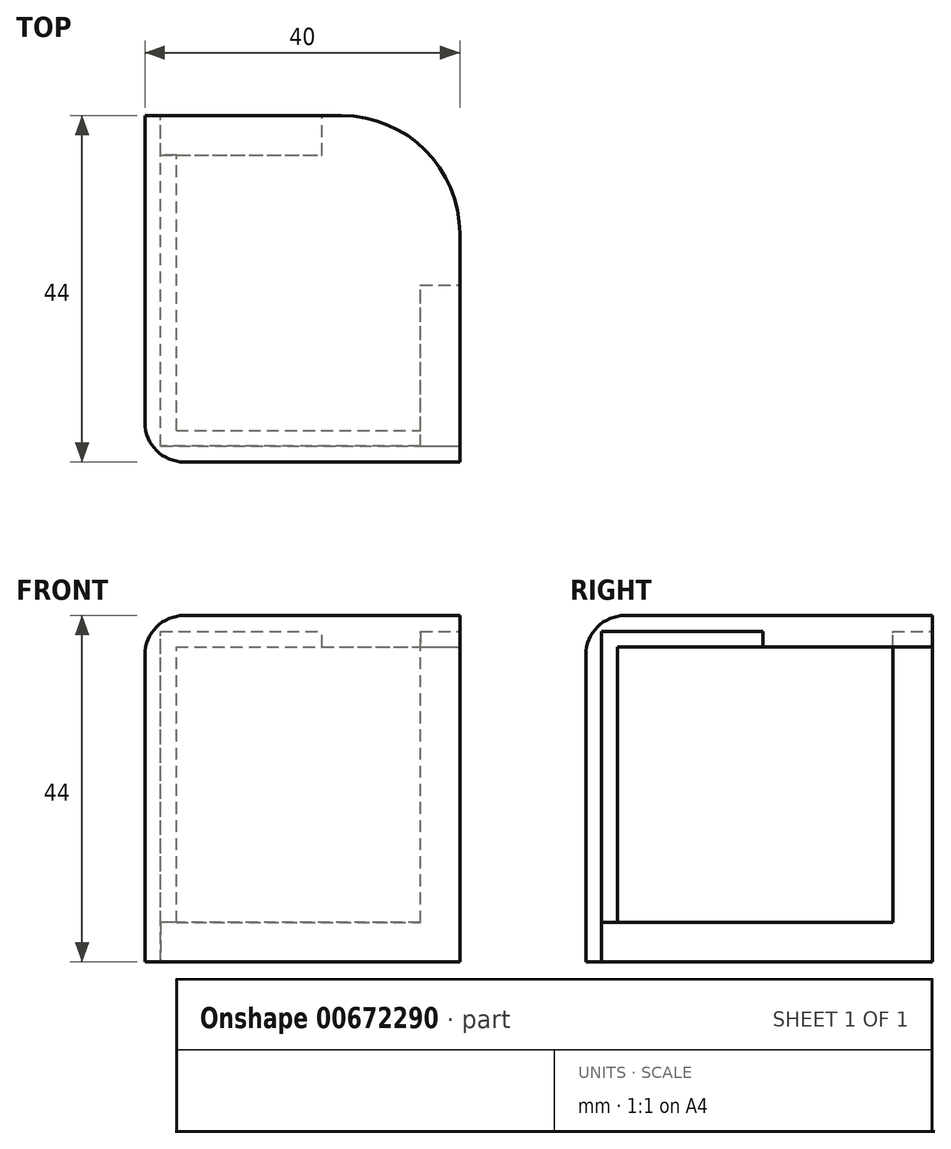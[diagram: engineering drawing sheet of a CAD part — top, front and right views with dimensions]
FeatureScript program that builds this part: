
annotation { "Feature Type Name" : "Feature", "Feature Type Description" : "" }
export const myFeature = defineFeature(function(context is Context, id is Id, definition is map)
    precondition{}
    {
        {
            var Q0;
            Q0=qCreatedBy(makeId("Top.planeOp"),FACE);
            var sketch = newSketch(context, id + "F0", { "sketchPlane" : qUnion([Q0])});
            skLineSegment(sketch, "E0", {"start": v(0, 0) * mm, "end": v(40, 0) * mm});
            skLineSegment(sketch, "E1", {"start": v(0, 44) * mm, "end": v(0, 0) * mm});
            skLineSegment(sketch, "E2", {"start": v(40, 0) * mm, "end": v(40, 44) * mm});
            skLineSegment(sketch, "E3", {"start": v(40, 44) * mm, "end": v(0, 44) * mm});
            skSolve(sketch);
        }
        {
            var Q0;
            Q0=makeQuery(id+"F0.imprint","IMPRINT",FACE,{"disambiguationData":[TD([[makeQuery(id+"F0.imprint","IMPRINT",EDGE,{"derivedFrom":sQuery(id+"F0.wireOp",EDGE,"E0")}),1.0]])]});
            extrude(context, id + "F1", {"entities" : qUnion([Q0]), "depth" : 44 * mm, "offsetDistance" : 25 * mm});
        }
        {
            var Q0;
            Q0=makeQuery(id+"F1.opExtrude","SWEPT_FACE",FACE,{"disambiguationData":[OSD([sQuery(id+"F0.wireOp",EDGE,"E2")])]});
            var sketch = newSketch(context, id + "F2", { "sketchPlane" : qUnion([Q0])});
            skLineSegment(sketch, "E4", {"start": v(4, 0) * mm, "end": v(4, 40) * mm});
            skLineSegment(sketch, "E5", {"start": v(4, 40) * mm, "end": v(44, 40) * mm});
            skSolve(sketch);
        }
        {
            var Q0;
            {var subQ0=sQuery(id+"F2.wireOp",EDGE,"E4");Q0=makeQuery(id+"F2.imprint","IMPRINT",FACE,{"disambiguationData":[TD([[makeQuery(id+"F2.imprint","IMPRINT",EDGE,{"derivedFrom":subQ0}),-1.0]])]});}
            extrude(context, id + "F3", {"entities" : qUnion([Q0]), "operationType" : NewBodyOperationType.REMOVE, "oppositeDirection" : true, "depth" : 36 * mm, "offsetDistance" : 25 * mm});
        }
        {
            var Q0;
            Q0=makeQuery(id+"F1.opExtrude","SWEPT_FACE",FACE,{"disambiguationData":[OSD([sQuery(id+"F0.wireOp",EDGE,"E2")])]});
            var sketch = newSketch(context, id + "F4", { "sketchPlane" : qUnion([Q0])});
            skLineSegment(sketch, "E6", {"start": v(2, 0) * mm, "end": v(2, 42) * mm});
            skLineSegment(sketch, "E7", {"start": v(2, 42) * mm, "end": v(44, 42) * mm});
            skLineSegment(sketch, "E8", {"start": v(22.5, 42) * mm, "end": v(22.5, 40) * mm});
            skSolve(sketch);
        }
        {
            var Q0;
            Q0 = qSketchRegion(id + "F4", true);
            var Q1;
            {var subQ3=sQuery(id+"F4.wireOp",EDGE,"E6");Q1=makeQuery(id+"F4.imprint","IMPRINT",FACE,{"disambiguationData":[TD([[makeQuery(id+"F4.imprint","IMPRINT",EDGE,{"derivedFrom":subQ3}),-1.0]])]});}
            extrude(context, id + "F5", {"entities" : qUnion([Q0, Q1]), "operationType" : NewBodyOperationType.REMOVE, "oppositeDirection" : true, "depth" : 5 * mm, "offsetDistance" : 25 * mm});
        }
        {
            var Q0;
            Q0=makeQuery(id+"F1.opExtrude","SWEPT_FACE",FACE,{"disambiguationData":[OSD([sQuery(id+"F0.wireOp",EDGE,"E3")])]});
            var sketch = newSketch(context, id + "F6", { "sketchPlane" : qUnion([Q0])});
            skLineSegment(sketch, "E9", {"start": v(-35, 0) * mm, "end": v(-2, 0) * mm});
            skLineSegment(sketch, "E10", {"start": v(-2, 0) * mm, "end": v(-2, 0) * mm});
            skLineSegment(sketch, "E11", {"start": v(-22.5, 40) * mm, "end": v(-22.5, 42) * mm});
            skLineSegment(sketch, "E12", {"start": v(-2, 0) * mm, "end": v(-2, 42) * mm});
            skLineSegment(sketch, "E13", {"start": v(-2, 42) * mm, "end": v(-22.5, 42) * mm});
            skSolve(sketch);
        }
        {
            var Q0;
            Q0 = qSketchRegion(id + "F6", true);
            var Q1;
            {var subQ1=sQuery(id+"F6.wireOp",EDGE,"E10");Q1=makeQuery(id+"F6.imprint","IMPRINT",FACE,{"disambiguationData":[TD([[makeQuery(id+"F6.imprint","IMPRINT",EDGE,{"derivedFrom":subQ1}),-1.0]])]});}
            var Q2;
            {var subQ1=sQuery(id+"F6.wireOp",EDGE,"E11");Q2=makeQuery(id+"F6.imprint","IMPRINT",FACE,{"disambiguationData":[TD([[makeQuery(id+"F6.imprint","IMPRINT",EDGE,{"derivedFrom":subQ1}),-1.0]])]});}
            extrude(context, id + "F7", {"entities" : qUnion([Q0, Q1, Q2]), "operationType" : NewBodyOperationType.REMOVE, "oppositeDirection" : true, "depth" : 5 * mm, "offsetDistance" : 25 * mm});
        }
        {
            var Q0;
            Q0=makeQuery(id+"F1.opExtrude","SWEPT_EDGE",EDGE,{"disambiguationData":[OSD([sQuery(id+"F0.wireOp",EDGE,"E2"),sQuery(id+"F0.wireOp",EDGE,"E3")])]});
            fillet(context, id + "F8", {"entities" : qUnion([Q0]), "radius" : 15 * mm, "tangentPropagation" : true, "allowEdgeOverflow" : false});
        }
        {
            var Q0;
            Q0=makeQuery(id+"F1.opExtrude","CAP_EDGE",EDGE,{"disambiguationData":[OSD([sQuery(id+"F0.wireOp",EDGE,"E1")])],"isStart":false});
            var Q1;
            Q1=makeQuery(id+"F1.opExtrude","CAP_EDGE",EDGE,{"disambiguationData":[OSD([sQuery(id+"F0.wireOp",EDGE,"E0")])],"isStart":false});
            var Q2;
            Q2=makeQuery(id+"F1.opExtrude","SWEPT_EDGE",EDGE,{"disambiguationData":[OSD([sQuery(id+"F0.wireOp",EDGE,"E0"),sQuery(id+"F0.wireOp",EDGE,"E1")])]});
            fillet(context, id + "F9", {"entities" : qUnion([Q0, Q1, Q2]), "radius" : 5 * mm, "tangentPropagation" : true, "allowEdgeOverflow" : false});
        }
        {
            var Q0;
            Q0=makeQuery(id+"F1.opExtrude","CAP_FACE",FACE,{"disambiguationData":[OSD([sQuery(id+"F0.wireOp",EDGE,"E0"),sQuery(id+"F0.wireOp",EDGE,"E1"),sQuery(id+"F0.wireOp",EDGE,"E2"),sQuery(id+"F0.wireOp",EDGE,"E3")])],"isStart":true});
            var sketch = newSketch(context, id + "F10", { "sketchPlane" : qUnion([Q0])});
            skLineSegment(sketch, "E14", {"start": v(35, -2) * mm, "end": v(2, -2) * mm});
            skLineSegment(sketch, "E15", {"start": v(2, -2) * mm, "end": v(2, -39) * mm});
            skSolve(sketch);
        }
        {
            var Q0;
            Q0 = qSketchRegion(id + "F10", true);
            var Q1;
            Q1=makeQuery(id+"F10.imprint","IMPRINT",FACE,{"disambiguationData":[TD([[makeQuery(id+"F10.imprint","IMPRINT",EDGE,{"derivedFrom":sQuery(id+"F10.wireOp",EDGE,"E14")}),1.0]])]});
            extrude(context, id + "F11", {"entities" : qUnion([Q0, Q1]), "operationType" : NewBodyOperationType.REMOVE, "oppositeDirection" : true, "depth" : 5 * mm, "offsetDistance" : 25 * mm});
        }
    });
